# Revit family: backflow_preventer-dc-zurn_wilkins-model_450_450G-(212-3_inch)
name_source: partatom
category: Pipe Accessories
units: mm (PartAtom-declared; Revit-internal decimal feet)

## family parameters
Always vertical = Yes
Cut with Voids When Loaded = No
OmniClass Number = 23.65.55.14.21
OmniClass Title = Non-Return Valves for Liquid Services
Part Type = Valve - Breaks Into
Round Connector Dimension = Use Radius
Shared = No
Work Plane-Based = No

## types (4) — shared parameters
Assembly Code = D2020300
Coupling Thickness = 0' - 1"
DIM D Center to Coupling End = 0' - 3 3/4"
Default Elevation = 0' - 0"
Description = Double Check Valve Assembly
Flange Thickness = 0' - 0 11/16"
Flow Rate (GPM) = 0 GPM
Hydrostatic Test Pressure = 350.00 psi
Main Material = Paint - Zurn - Ductile Iron
Manufacturer = Zurn Water, LLC
Manufacturer Brand = Zurn Wilkins
Max Working Water Pressure = 175.00 psi
Max Working Water Temperature = 140 °F
Modified Date = 10/23/2025
Product Documentation Link = https://files.zurn.com
Product Installation Sheet URL = https://files.zurn.com
Product Page URL = https://www.zurn.com
Product data url = https://www.bimobject.com
Repair Parts URL = https://files.zurn.com
URL = https://www.zurn.com

## per-type parameters (varying)
- 212-450 (2-1/2" 450): Access Panel Radius=0' - 3 13/16"; Body Large Radius=0' - 2 13/16"; Body Size Factor=0' - 2 1/2"; Body Small Radius=0' - 1 3/4"; Body Sub A=0' - 6 11/32"; Body Top radius=0' - 2 1/2"; DIM A Length=2' - 2"; DIM B Overall Height=1' - 8 1/2"; DIM C Body center to Gate end=0' - 11 3/8"; Elbow=Zurn - Flange - Elbow 450 2.5 NRS : 2.5; Elbow Length=0' - 5 1/16"; Flange Diameter=0' - 7"; Gate Length=0' - 7 1/2"; Gate Valve Distance=0' - 8 1/2"; Gate valve=Gate Valve_450 2.5in NRS : 2 1/2"; Height=1' - 8 1/2"; Length=2' - 2"; Main Body Length=1' - 3 7/8"; Model=450; Nominal Diameter=0' - 2 1/2"; Nominal Radius=0' - 1 1/4"; Pressure Loss at Rated Flow=8.40 psi; Product Weight (lbs)=182; Rated Flow=225 GPM; Relief valve loction=0' - 8 1/16"; Tesk Cock Height=0' - 6"; Test Cock Center Height=0' - 3 3/8"; Test Cock First Position=0' - 1 5/8"; Test Cock Second Position=0' - 11 3/4"
- 3-450 (3" 450): Access Panel Radius=0' - 3 29/32"; Body Large Radius=0' - 3 3/16"; Body Size Factor=0' - 3"; Body Small Radius=0' - 2"; Body Sub A=0' - 6 1/2"; Body Top radius=0' - 2 3/4"; DIM A Length=2' - 3"; DIM B Overall Height=1' - 9 1/2"; DIM C Body center to Gate end=1' - 0 3/8"; Elbow=Zurn - Flange - Elbow 450 2.5 NRS : 3"; Elbow Length=0' - 5 9/16"; Flange Diameter=0' - 7 1/2"; Gate Length=0' - 8"; Gate Valve Distance=0' - 9 1/2"; Gate valve=Gate Valve_450 2.5in NRS : 3"; Height=1' - 9 1/2"; Length=2' - 3"; Main Body Length=1' - 7 1/2"; Model=450; Nominal Diameter=0' - 3"; Nominal Radius=0' - 1 1/2"; Pressure Loss at Rated Flow=8.20 psi; Product Weight (lbs)=207; Rated Flow=320 GPM; Relief valve loction=0' - 8 5/8"; Tesk Cock Height=0' - 8"; Test Cock Center Height=0' - 3"; Test Cock First Position=0' - 1 7/8"; Test Cock Second Position=1' - 2"
- 3-450G (3" 450G): Access Panel Radius=0' - 3 29/32"; Body Large Radius=0' - 3 3/16"; Body Size Factor=0' - 3"; Body Small Radius=0' - 2"; Body Sub A=0' - 6 1/2"; Body Top radius=0' - 2 3/4"; DIM A Length=2' - 3"; DIM B Overall Height=1' - 9 1/2"; DIM C Body center to Gate end=1' - 0 3/8"; Elbow=Zurn - Flange - Elbow 450 2.5 NRS : 3"; Elbow Length=0' - 5 9/16"; Flange Diameter=0' - 7 1/2"; Gate Length=0' - 8"; Gate Valve Distance=0' - 0"; Gate valve=Gate Valve_450 2.5in NRS : 3" G; Height=1' - 9 1/2"; Length=2' - 3"; Main Body Length=1' - 7 1/2"; Model=450G; Nominal Diameter=0' - 3"; Nominal Radius=0' - 1 1/2"; Pressure Loss at Rated Flow=8.20 psi; Product Weight (lbs)=207; Rated Flow=320 GPM; Relief valve loction=0' - 8 5/8"; Tesk Cock Height=0' - 8"; Test Cock Center Height=0' - 3"; Test Cock First Position=0' - 1 7/8"; Test Cock Second Position=1' - 2"
- 212-450G (2-1/2" 450G): Access Panel Radius=0' - 3 13/16"; Body Large Radius=0' - 2 13/16"; Body Size Factor=0' - 2 1/2"; Body Small Radius=0' - 1 3/4"; Body Sub A=0' - 6 11/32"; Body Top radius=0' - 2 1/2"; DIM A Length=2' - 2"; DIM B Overall Height=1' - 8 1/2"; DIM C Body center to Gate end=0' - 11 3/8"; Elbow=Zurn - Flange - Elbow 450 2.5 NRS : 2.5; Elbow Length=0' - 5 1/16"; Flange Diameter=0' - 7"; Gate Length=0' - 7 1/2"; Gate Valve Distance=0' - 0"; Gate valve=Gate Valve_450 2.5in NRS : 2 1/2" G; Height=1' - 8 1/2"; Length=2' - 2"; Main Body Length=1' - 3 7/8"; Model=450G; Nominal Diameter=0' - 2 1/2"; Nominal Radius=0' - 1 1/4"; Pressure Loss at Rated Flow=8.40 psi; Product Weight (lbs)=182; Rated Flow=225 GPM; Relief valve loction=0' - 8 1/16"; Tesk Cock Height=0' - 6"; Test Cock Center Height=0' - 3 3/8"; Test Cock First Position=0' - 1 5/8"; Test Cock Second Position=0' - 11 3/4"

## geometry (parser evidence)
native form markers: Sweep x14
no freeform markers — native parametric forms only
